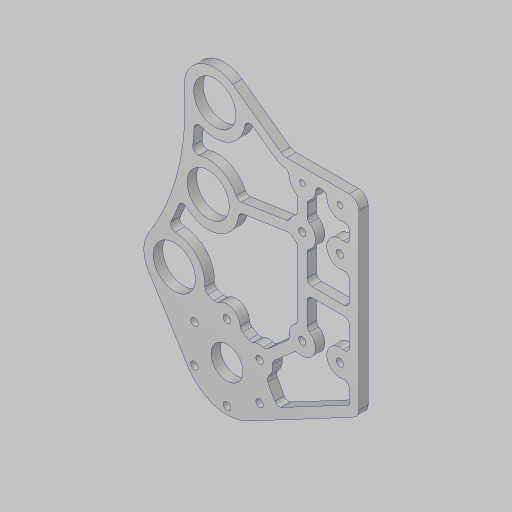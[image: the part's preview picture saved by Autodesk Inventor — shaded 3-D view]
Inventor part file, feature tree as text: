
AUTODESK INVENTOR PART (.ipt)
format: ipt  version: 2023.5 (Build 275446000, 446)  size: 445,440 bytes
history: native  units: in
note: dims shown in document units (in); Inventor stores cm internally (conversion verified against a paired STEP export)
features: sketch x4, hole x3, extrude x2, fillet x2, projected_geometry x2
ambient origin geometry x8: Origin, YZ Plane, XZ Plane, XY Plane, X Axis, Y Axis, Z Axis, Center Point
bodies: Solid1 (feature_tree)
feature tree (13):
  sketch  "Sketch1"  dims[d0=2.0in d1=15.0in]
  sketch  "Sketch2"  dims[d2=0.875in d3=17.0in d4=2.0in]
  extrude  "Extrusion1"  Depth=2.0in
  hole  "Hole1"  [1 undecoded]
  fillet  "Fillet1"  Radius=2.0in
  hole  "Hole2"  [1 undecoded]
  hole  "Hole3"  [1 undecoded]
  extrude  "Extrusion2"  Depth=0.25in
  fillet  "Fillet2"  Radius=3.6in
  sketch  "Sketch3"  dims[d5=17.0in d6=1.0in]
  projected_geometry  "Projected Loop1"
  sketch  "Sketch4"  dims[d7=0.2405in d8=2.4in d9=0.5in d10=3.6in d11=1.5in d12=1.5in d13=0.9in d14=3.7in d15=1.0in d16=3.4in d17=3.0in d20=2.0in d22=1.125in d23=4.297in d24=0.25in d25=2.0in d26=2.3622in d28=360.0deg d30=7.0in d31=2.0in d32=0.201in d33=1.0in d34=1.5in d35=1.0in d36=0.201in d37=1.0in d38=1.0in d39=2.5in d40=0.25in d41=0.0in d42=0.85in d43=0.201in d44=0.75in d45=0.385in d46=0.25in d47=0.5635in d48=1.0in d49=0.8108in d50=0.375in d51=0.26in d52=1.825in d53=0.156in d54=0.38in d55=0.385in d56=0.25in d57=0.5635in d58=1.0in d59=0.8108in d60=0.25in d61=0.25in d62=0.25in d63=0.25in d64=0.25in d65=0.25in d66=0.125in d67=0.125in d68=0.125in d69=0.125in d70=2.5in d71=0.125in d72=0.125in d73=0.125in d74=0.125in d75=1.0in d76=0.0in d77=0.0in d78=0.13in d81=1.75in d82=0.875in d83=0.156in d84=0.38in d85=0.375in d86=0.25in d87=0.5635in d88=1.0in d89=0.8108in d90=0.125in d91=0.125in]
  projected_geometry  "Projected Loop2"
note: 3 required parameter values undecoded (feature->parameter linkage not recoverable at this tier; creation-order binding heuristic only, values carry confidence <= 0.55)
